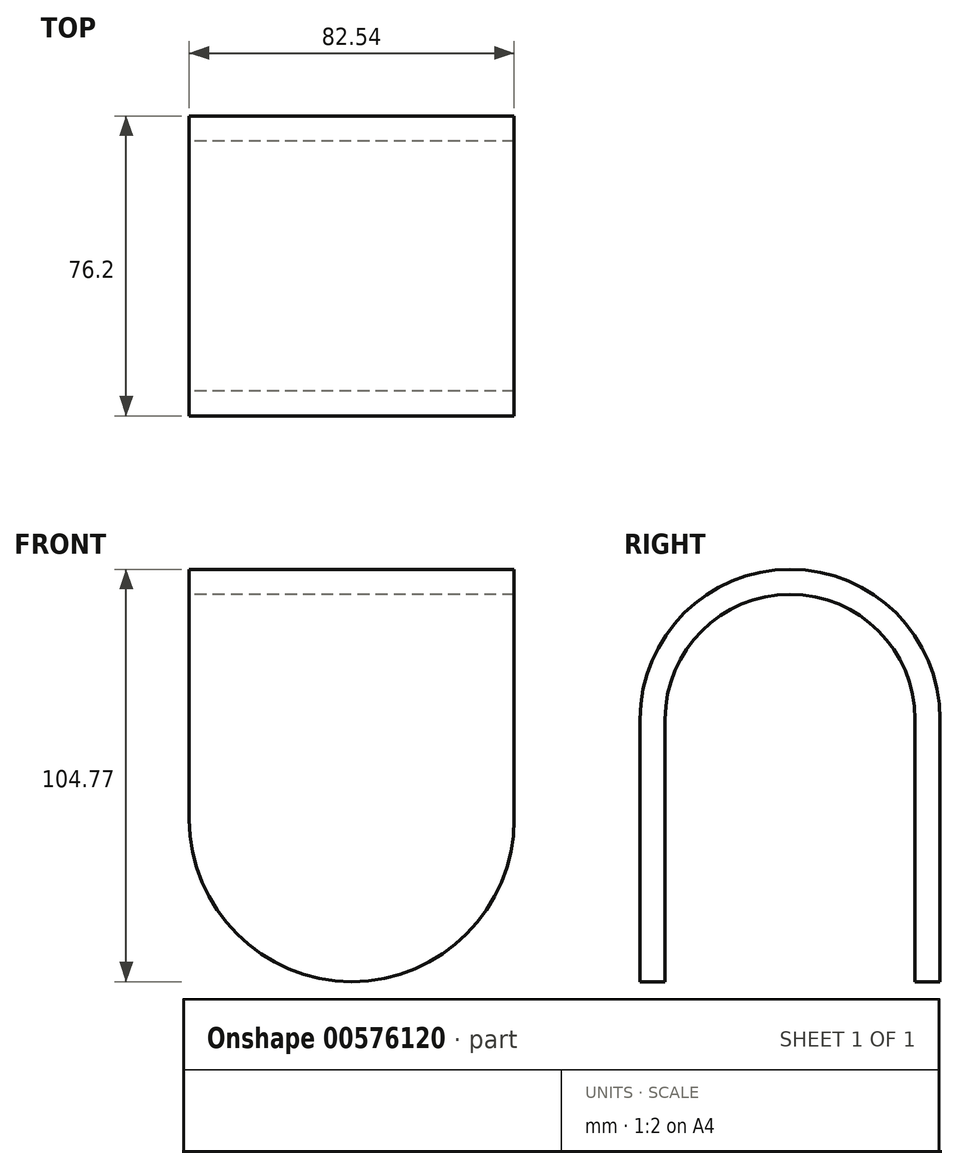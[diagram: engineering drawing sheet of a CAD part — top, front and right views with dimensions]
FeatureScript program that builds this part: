
annotation { "Feature Type Name" : "Feature", "Feature Type Description" : "" }
export const myFeature = defineFeature(function(context is Context, id is Id, definition is map)
    precondition{}
    {
        {
            var Q0;
            Q0=qCreatedBy(makeId("Right.planeOp"),FACE);
            var sketch = newSketch(context, id + "F0", { "sketchPlane" : qUnion([Q0])});
            skArc(sketch, "E0", {"start": v(-38.1, 0) * mm, "mid": v(0, 38.1) * mm, "end": v(38.1, 0) * mm});
            skLineSegment(sketch, "E1", {"start": v(-38.1, 0) * mm, "end": v(-38.1, -66.68) * mm});
            skLineSegment(sketch, "E2", {"start": v(38.1, 0) * mm, "end": v(38.1, -66.68) * mm});
            skLineSegment(sketch, "E3.0", {"start": v(-31.75, 0) * mm, "end": v(-31.75, -66.67) * mm});
            skArc(sketch, "E3.1", {"start": v(-31.75, 0) * mm, "mid": v(0, 31.75) * mm, "end": v(31.75, 0) * mm});
            skLineSegment(sketch, "E3.2", {"start": v(31.75, 0) * mm, "end": v(31.75, -66.68) * mm});
            skLineSegment(sketch, "E4", {"start": v(-38.1, -66.68) * mm, "end": v(-31.75, -66.68) * mm});
            skLineSegment(sketch, "E5", {"start": v(31.75, -66.68) * mm, "end": v(38.1, -66.68) * mm});
            skSolve(sketch);
        }
        {
            var Q0;
            Q0 = qSketchRegion(id + "F0", true);
            extrude(context, id + "F1", {"entities" : qUnion([Q0]), "endBound" : BoundingType.SYMMETRIC, "depth" : 82.55 * mm, "offsetDistance" : 25.4 * mm});
        }
        {
            var Q0;
            Q0=makeQuery(id+"F1.opExtrude","CAP_EDGE",EDGE,{"disambiguationData":[OSD([sQuery(id+"F0.wireOp",EDGE,"E5")])],"isStart":true});
            var Q1;
            Q1=makeQuery(id+"F1.opExtrude","CAP_EDGE",EDGE,{"disambiguationData":[OSD([sQuery(id+"F0.wireOp",EDGE,"E4")])],"isStart":true});
            var Q2;
            Q2=makeQuery(id+"F1.opExtrude","CAP_EDGE",EDGE,{"disambiguationData":[OSD([sQuery(id+"F0.wireOp",EDGE,"E4")])],"isStart":false});
            var Q3;
            Q3=makeQuery(id+"F1.opExtrude","CAP_EDGE",EDGE,{"disambiguationData":[OSD([sQuery(id+"F0.wireOp",EDGE,"E5")])],"isStart":false});
            fillet(context, id + "F2", {"entities" : qUnion([Q0, Q1, Q2, Q3]), "radius" : 41.27 * mm, "tangentPropagation" : true, "allowEdgeOverflow" : false});
        }
    });
